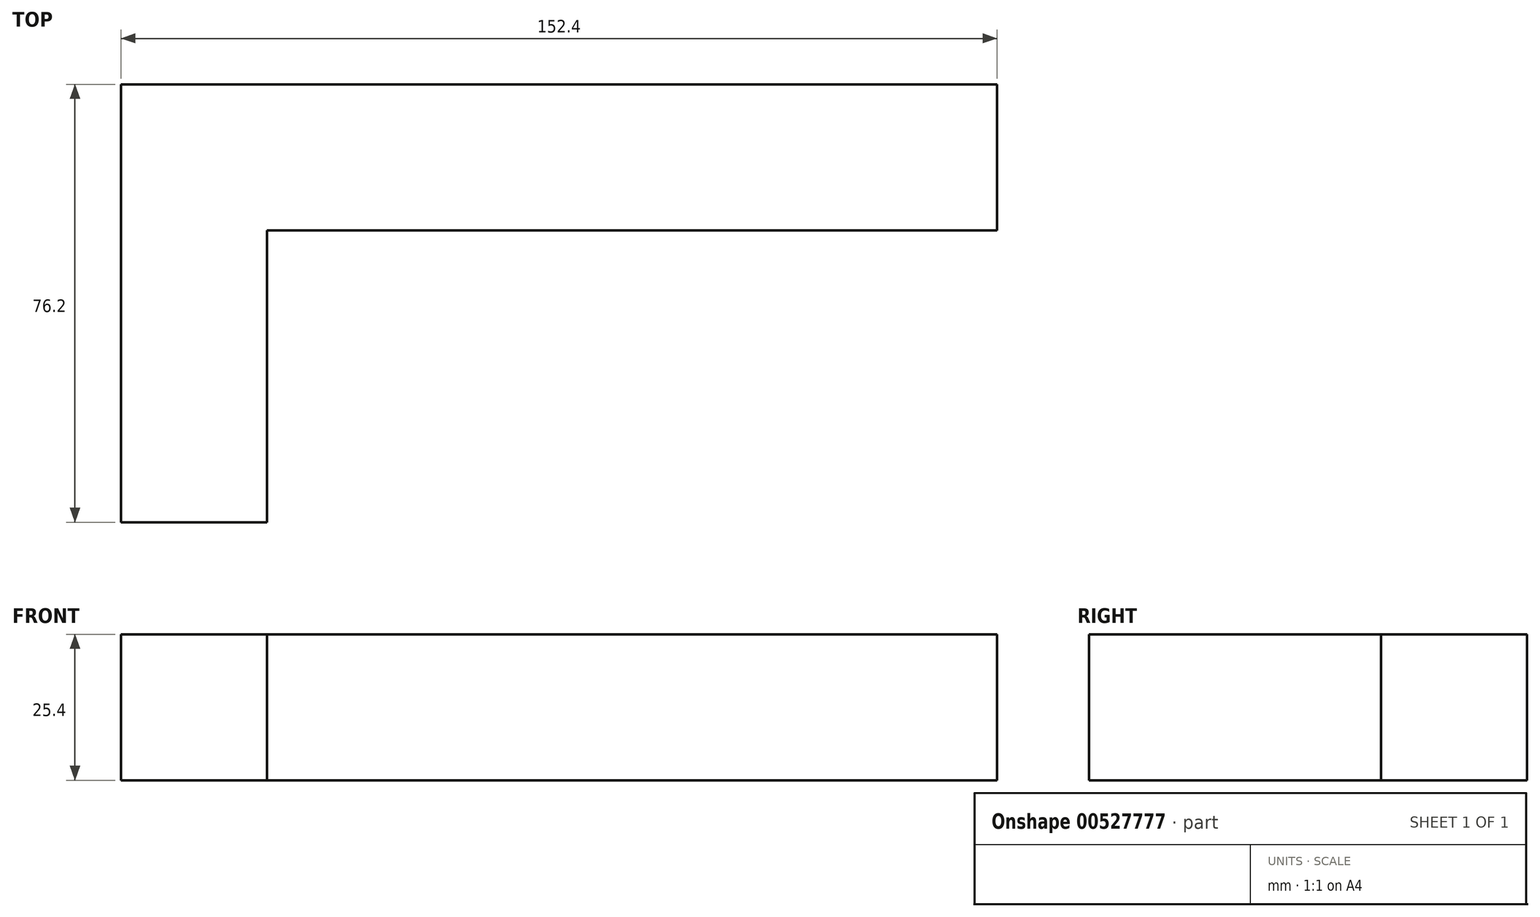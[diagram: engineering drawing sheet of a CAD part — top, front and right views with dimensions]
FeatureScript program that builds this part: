
annotation { "Feature Type Name" : "Feature", "Feature Type Description" : "" }
export const myFeature = defineFeature(function(context is Context, id is Id, definition is map)
    precondition{}
    {
        {
            var Q0;
            Q0=qCreatedBy(makeId("Top.planeOp"),FACE);
            var sketch = newSketch(context, id + "F0", { "sketchPlane" : qUnion([Q0])});
            skLineSegment(sketch, "E0", {"start": v(-86.88, 25.08) * mm, "end": v(-86.88, -51.12) * mm});
            skLineSegment(sketch, "E1", {"start": v(-86.88, -51.12) * mm, "end": v(-61.48, -51.12) * mm});
            skLineSegment(sketch, "E2", {"start": v(-61.48, -51.12) * mm, "end": v(-61.48, -0.32) * mm});
            skLineSegment(sketch, "E3", {"start": v(-61.48, -0.32) * mm, "end": v(65.52, -0.32) * mm});
            skLineSegment(sketch, "E4", {"start": v(65.52, -0.32) * mm, "end": v(65.52, 25.08) * mm});
            skLineSegment(sketch, "E5", {"start": v(65.52, 25.08) * mm, "end": v(-86.88, 25.08) * mm});
            skLineSegment(sketch, "E6.bottom", {"start": v(14.72, 25.08) * mm, "end": v(65.52, 25.08) * mm});
            skLineSegment(sketch, "E6.top", {"start": v(14.72, -0.32) * mm, "end": v(65.52, -0.32) * mm});
            skLineSegment(sketch, "E6.left", {"start": v(14.72, 25.08) * mm, "end": v(14.72, -0.32) * mm});
            skLineSegment(sketch, "E6.right", {"start": v(65.52, 25.08) * mm, "end": v(65.52, -0.32) * mm});
            skSolve(sketch);
        }
        {
            var Q0;
            Q0 = qSketchRegion(id + "F0", true);
            extrude(context, id + "F1", {"entities" : qUnion([Q0]), "depth" : 25.4 * mm, "offsetDistance" : 25.4 * mm});
        }
    });
